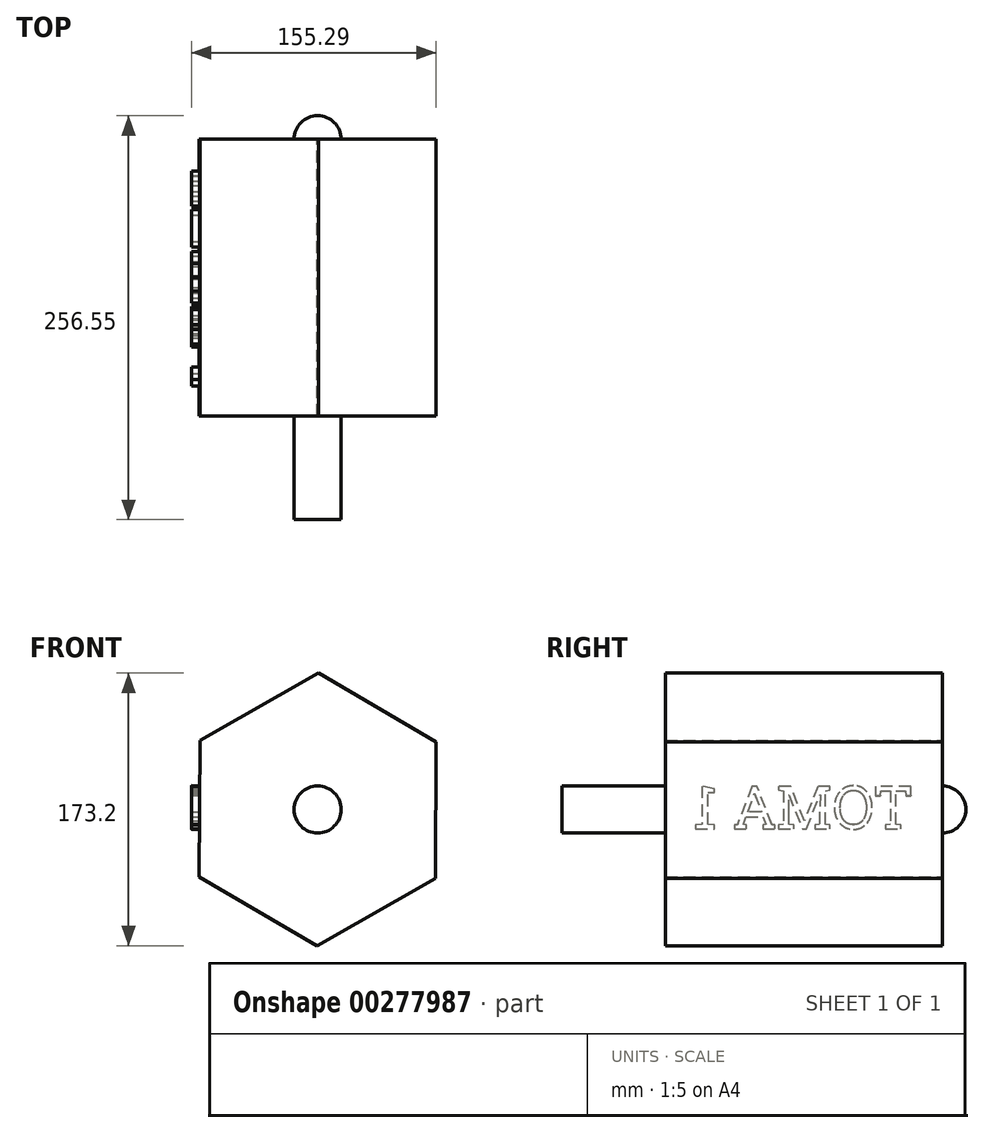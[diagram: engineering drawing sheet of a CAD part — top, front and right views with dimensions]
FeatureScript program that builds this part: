
annotation { "Feature Type Name" : "Feature", "Feature Type Description" : "" }
export const myFeature = defineFeature(function(context is Context, id is Id, definition is map)
    precondition{}
    {
        {
            var Q0;
            Q0=qCreatedBy(makeId("Front.planeOp"),FACE);
            var sketch = newSketch(context, id + "F0", { "sketchPlane" : qUnion([Q0])});
            skCircle(sketch, "E0.cCircle", {"center": v(0, 0) * mm, "radius": 75 * mm, "construction": true});
            skLineSegment(sketch, "E0.0", {"start": v(74.78, -43.69) * mm, "end": v(-0.45, -86.6) * mm});
            skLineSegment(sketch, "E0.1", {"start": v(-0.45, -86.6) * mm, "end": v(-75.22, -42.91) * mm});
            skLineSegment(sketch, "E0.2", {"start": v(-75.22, -42.91) * mm, "end": v(-74.78, 43.69) * mm});
            skLineSegment(sketch, "E0.3", {"start": v(-74.78, 43.69) * mm, "end": v(0.45, 86.6) * mm});
            skLineSegment(sketch, "E0.4", {"start": v(0.45, 86.6) * mm, "end": v(75.22, 42.91) * mm});
            skLineSegment(sketch, "E0.5", {"start": v(75.22, 42.91) * mm, "end": v(74.78, -43.69) * mm});
            skPoint(sketch, "E0.0.midPoint", {"position": v(37.16, -65.14) * mm});
            skSolve(sketch);
        }
        {
            var Q0;
            Q0 = qSketchRegion(id + "F0", true);
            extrude(context, id + "F1", {"entities" : qUnion([Q0]), "depth" : 175.77 * mm});
        }
        {
            var Q0;
            Q0=makeQuery(id+"F1.opExtrude","CAP_FACE",FACE,{"disambiguationData":[OSD([sQuery(id+"F0.wireOp",EDGE,"E0.0"),sQuery(id+"F0.wireOp",EDGE,"E0.1"),sQuery(id+"F0.wireOp",EDGE,"E0.2"),sQuery(id+"F0.wireOp",EDGE,"E0.3"),sQuery(id+"F0.wireOp",EDGE,"E0.4"),sQuery(id+"F0.wireOp",EDGE,"E0.5")])],"isStart":false});
            var sketch = newSketch(context, id + "F2", { "sketchPlane" : qUnion([Q0])});
            skCircle(sketch, "E1", {"center": v(0, 0) * mm, "radius": 15 * mm});
            skSolve(sketch);
        }
        {
            var Q0;
            Q0=makeQuery(id+"F2.imprint","IMPRINT",FACE,{"disambiguationData":[TD([[makeQuery(id+"F2.imprint","IMPRINT",EDGE,{"derivedFrom":sQuery(id+"F2.wireOp",EDGE,"E1")}),1.0]])]});
            extrude(context, id + "F3", {"entities" : qUnion([Q0]), "operationType" : NewBodyOperationType.ADD, "depth" : 65.8 * mm});
        }
        {
            var Q0;
            Q0=makeQuery(id+"F1.opExtrude","CAP_FACE",FACE,{"disambiguationData":[OSD([sQuery(id+"F0.wireOp",EDGE,"E0.0"),sQuery(id+"F0.wireOp",EDGE,"E0.1"),sQuery(id+"F0.wireOp",EDGE,"E0.2"),sQuery(id+"F0.wireOp",EDGE,"E0.3"),sQuery(id+"F0.wireOp",EDGE,"E0.4"),sQuery(id+"F0.wireOp",EDGE,"E0.5")])],"isStart":true});
            var sketch = newSketch(context, id + "F4", { "sketchPlane" : qUnion([Q0])});
            skCircle(sketch, "E2", {"center": v(0, 0) * mm, "radius": 15 * mm});
            skLineSegment(sketch, "E3", {"start": v(-15, 0) * mm, "end": v(15, 0) * mm});
            skLineSegment(sketch, "E4", {"start": v(0, 0) * mm, "end": v(30.6, 0) * mm, "construction": true});
            skSolve(sketch);
        }
        {
            var Q0;
            {var subQ0=sQuery(id+"F4.wireOp",EDGE,"E3");Q0=makeQuery(id+"F4.imprint","IMPRINT",FACE,{"disambiguationData":[TD([[makeQuery(id+"F4.imprint","IMPRINT",EDGE,{"derivedFrom":subQ0}),1.0]])]});}
            var Q1;
            Q1=sQuery(id+"F4.wireOp",EDGE,"E4");
            revolve(context, id + "F5", {"operationType" : NewBodyOperationType.ADD, "entities" : qUnion([Q0]), "axis" : qUnion([Q1]), "revolveType" : RevolveType.FULL});
        }
        {
            var Q0;
            Q0=makeQuery(id+"F1.opExtrude","SWEPT_FACE",FACE,{"disambiguationData":[OSD([sQuery(id+"F0.wireOp",EDGE,"E0.2")])]});
            var sketch = newSketch(context, id + "F6", { "sketchPlane" : qUnion([Q0])});
            skText(sketch, "E5", { "text": "TOMA 1", "fontName": "RobotoSlab-Regular.ttf"});
            const initialGuessF6  = {"E5": [0.01935, -0.01266, 1, 0, 0.02733]};
            skSetInitialGuess(sketch, initialGuessF6);
            skSolve(sketch);
        }
        {
            var Q0;
            Q0 = qSketchRegion(id + "F6", true);
            extrude(context, id + "F7", {"entities" : qUnion([Q0]), "operationType" : NewBodyOperationType.ADD, "depth" : 5 * mm});
        }
    });
